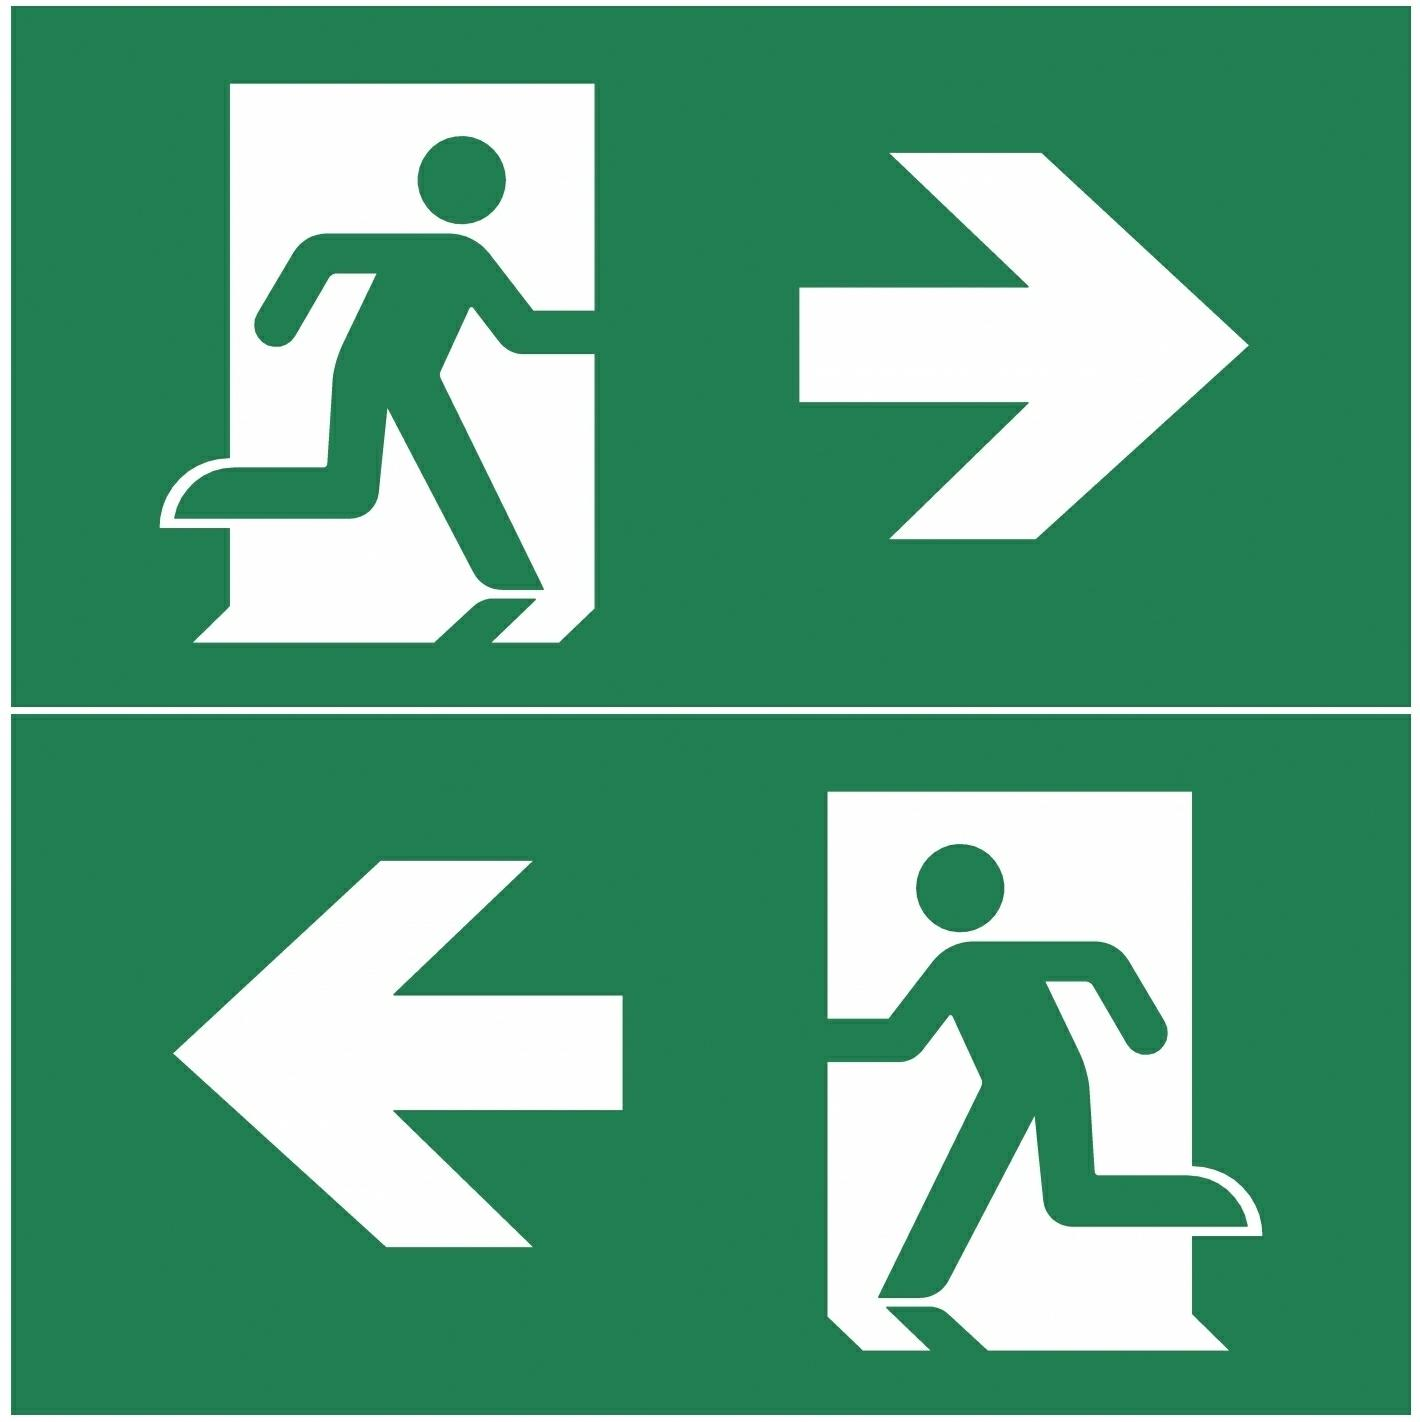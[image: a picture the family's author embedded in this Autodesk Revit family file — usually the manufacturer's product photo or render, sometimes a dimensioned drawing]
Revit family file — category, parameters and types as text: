
# Revit family: TWT8053WM
name_source: partatom
category: Lighting Fixtures
revit_build: Autodesk Revit 2016 (Build: 20150714_1515(x64)
units: mm (PartAtom-declared; Revit-internal decimal feet)

## family parameters
Always vertical = Yes
Cut with Voids When Loaded = No
Light Source = No
OmniClass Number = 23.80.70.00
OmniClass Title = Lighting
Part Type = Normal
Room Calculation Point = No
Round Connector Dimension = Use Diameter
Shared = No
Work Plane-Based = No

## types (6) — shared parameters
Body Material = Plastic
Color = RAL9003
Customs Code = 94056080
Description = Self-Contained LED Exit Light with 3 h Battery Backup and Self Testing
ETIM Product Class = EC001957
Electrical Installation = 2/3 x 2,5 mm² -o-
Feature = Lumi Test
GTIN Code = 6438045011844
Glow Wire Test of Plastic Materials = 650 °C
Height = 185 mm  [stored 0.606955 ft]
IP Class = IP44
Keynote = 23
Length = 268 mm  [stored 0.879265 ft]
Light Source = LED
Manufacturer = Teknoware Oy
Max Input Power VA = 5 VA
Model = ESC 80
Mounting_Optional = Recess, Flag, Pendel
Mounting_Standard = Wall, Ceiling
Nominal Supply Voltage = 220-240 V, 50/60 Hz AC
Product Code = TWT8053WM
Protection Class = II
Sähkönumero = 4211318
Sähkönumerot.fi -tuotesivu = http://www.sahkonumerot.fi
Temperature Range Min_Max = -5...+30 °C
Type Image = ESC80.jpg
URL = http://www.teknoware.com
Viewing Distance = 20000 mm  [stored 65.6168 ft]
Wattage Comments = LED
Weight = 0.80 kg
Width = 40 mm  [stored 0.131234 ft]

## per-type parameters (varying)
| type | Aperture for Recess Mounting | Max Input Power W | Pictogram Type |
| Arrow down 20m | 53 mm x 275 mm | 4 W | OPASTE PBV80202E |
| Arrow down 30m | 53 mm  x 275 mm | 0 W | OPASTE PBV80302E |
| Arrow down 26m | 53 mm x 275 mm | 4 W | OPASTE PBV80262E |
| Arrow left_right 20m | 53 mm x 275 mm | 4 W | OPASTE PBV80201E |
| Arrow left_right 26m | 53 mm x 275 mm | 4 W | OPASTE PBV80261E |
| Arrow left_right 30m | 53 mm x 275 mm | 4 W | OPASTE PBV80301E |

note: [stored X ft] marks values corroborated as IEEE doubles in the binary element streams (Revit-internal decimal feet)

## geometry (parser evidence)
native form markers: Sweep x24
no freeform markers — native parametric forms only
